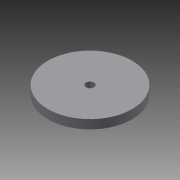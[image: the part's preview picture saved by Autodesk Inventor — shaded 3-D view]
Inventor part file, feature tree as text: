
AUTODESK INVENTOR PART (.ipt)
format: ipt  version: 2015 (Build 190159000, 159)  size: 73,728 bytes
history: native  units: mm
features: extrude x1, sketch x1
ambient origin geometry x8: Origin, YZ Plane, XZ Plane, XY Plane, X Axis, Y Axis, Z Axis, Center Point
bodies: Solid1 (feature_tree)
feature tree (2):
  extrude  "Extrusion1"  Depth=3.0mm
  sketch  "Sketch1"  dims[d0=28.5mm d3=2.8mm d4=3.0mm d5=0.0mm]
